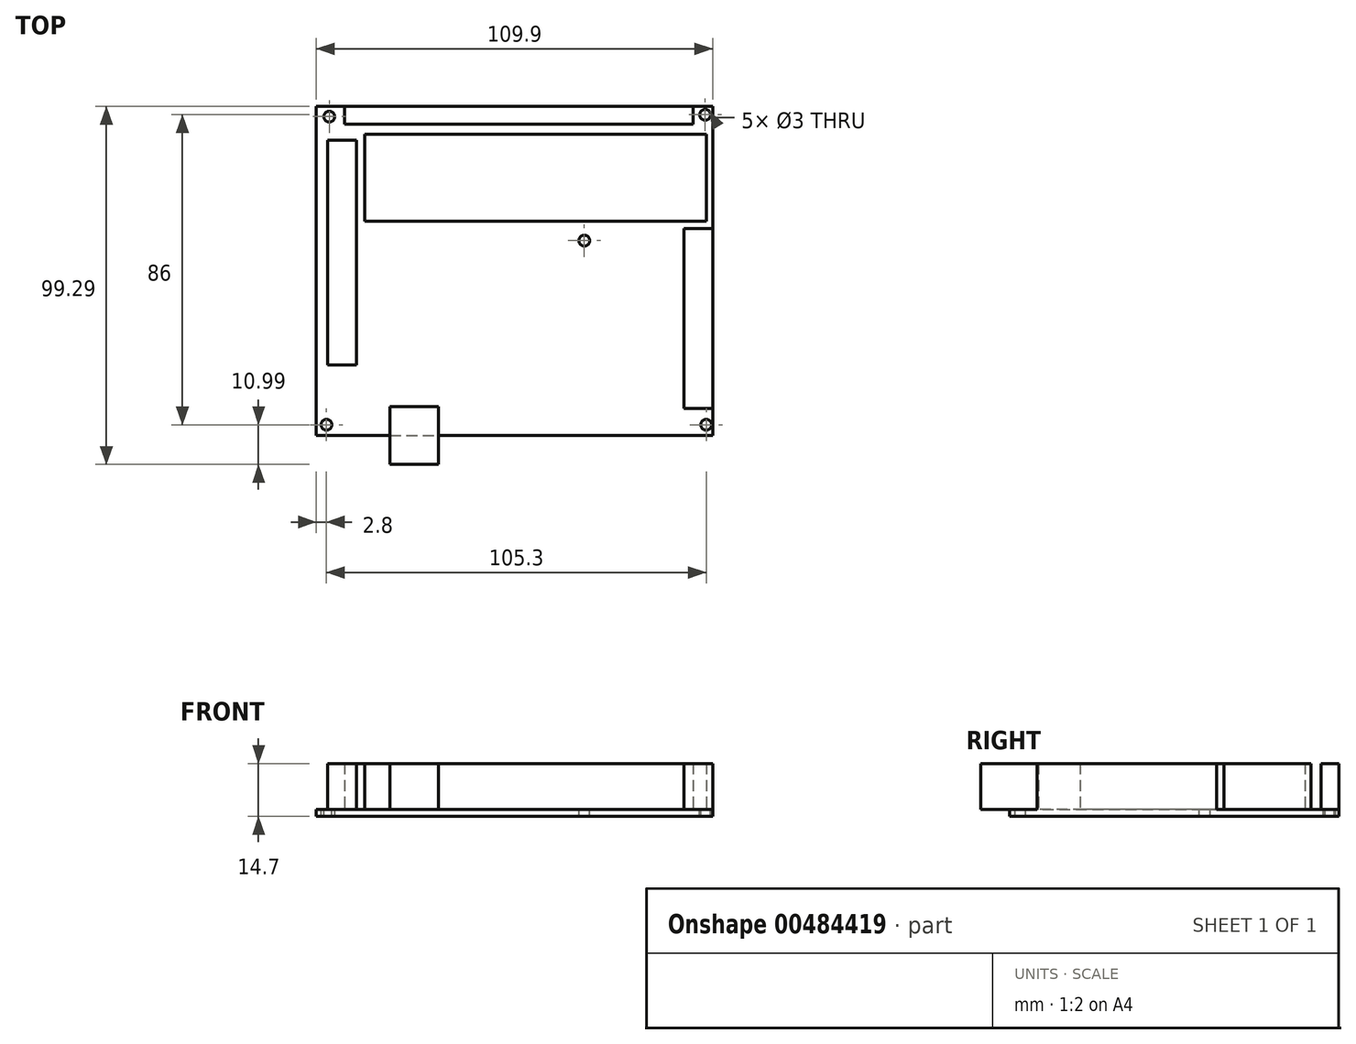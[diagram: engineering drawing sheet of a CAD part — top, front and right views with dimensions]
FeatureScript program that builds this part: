
annotation { "Feature Type Name" : "Feature", "Feature Type Description" : "" }
export const myFeature = defineFeature(function(context is Context, id is Id, definition is map)
    precondition{}
    {
        {
            var Q0;
            Q0=qCreatedBy(makeId("Top.planeOp"),FACE);
            var sketch = newSketch(context, id + "F0", { "sketchPlane" : qUnion([Q0])});
            skLineSegment(sketch, "E0.bottom", {"start": v(0, 0) * mm, "end": v(109.9, 0) * mm});
            skLineSegment(sketch, "E0.top", {"start": v(0, 91.3) * mm, "end": v(109.9, 91.3) * mm});
            skLineSegment(sketch, "E0.left", {"start": v(0, 0) * mm, "end": v(0, 91.3) * mm});
            skLineSegment(sketch, "E0.right", {"start": v(109.9, 0) * mm, "end": v(109.9, 91.3) * mm});
            skSolve(sketch);
        }
        {
            var Q0;
            Q0 = qSketchRegion(id + "F0", true);
            extrude(context, id + "F1", {"entities" : qUnion([Q0]), "depth" : 2 * mm, "offsetDistance" : 25.4 * mm});
        }
        {
            var Q0;
            Q0=makeQuery(id+"F1.opExtrude","CAP_FACE",FACE,{"disambiguationData":[OSD([sQuery(id+"F0.wireOp",EDGE,"E0.bottom"),sQuery(id+"F0.wireOp",EDGE,"E0.top"),sQuery(id+"F0.wireOp",EDGE,"E0.left"),sQuery(id+"F0.wireOp",EDGE,"E0.right")])],"isStart":false});
            var sketch = newSketch(context, id + "F2", { "sketchPlane" : qUnion([Q0])});
            skCircle(sketch, "E1", {"center": v(3.6, 88.5) * mm, "radius": 1.5 * mm});
            skCircle(sketch, "E2", {"center": v(108.1, 3) * mm, "radius": 1.5 * mm});
            skCircle(sketch, "E3", {"center": v(107.8, 89) * mm, "radius": 1.5 * mm});
            skCircle(sketch, "E4", {"center": v(2.8, 3) * mm, "radius": 1.5 * mm});
            skCircle(sketch, "E5", {"center": v(74.3, 54.1) * mm, "radius": 1.5 * mm});
            skSolve(sketch);
        }
        {
            var Q0;
            Q0 = qSketchRegion(id + "F2", true);
            extrude(context, id + "F3", {"entities" : qUnion([Q0]), "operationType" : NewBodyOperationType.REMOVE, "oppositeDirection" : true, "depth" : 25.4 * mm, "offsetDistance" : 25.4 * mm});
        }
        {
            var Q0;
            Q0=makeQuery(id+"F1.opExtrude","CAP_FACE",FACE,{"disambiguationData":[OSD([sQuery(id+"F0.wireOp",EDGE,"E0.bottom"),sQuery(id+"F0.wireOp",EDGE,"E0.top"),sQuery(id+"F0.wireOp",EDGE,"E0.left"),sQuery(id+"F0.wireOp",EDGE,"E0.right")])],"isStart":false});
            var sketch = newSketch(context, id + "F4", { "sketchPlane" : qUnion([Q0]), "disableImprinting" : false});
            skLineSegment(sketch, "E6.bottom", {"start": v(20.39, 8.06) * mm, "end": v(33.82, 8.06) * mm});
            skLineSegment(sketch, "E6.top", {"start": v(20.39, -7.99) * mm, "end": v(33.82, -7.99) * mm});
            skLineSegment(sketch, "E6.left", {"start": v(20.39, 8.06) * mm, "end": v(20.39, -7.99) * mm});
            skLineSegment(sketch, "E6.right", {"start": v(33.82, 8.06) * mm, "end": v(33.82, -7.99) * mm});
            skSolve(sketch);
        }
        {
            var Q0;
            Q0 = qSketchRegion(id + "F4", true);
            extrude(context, id + "F5", {"entities" : qUnion([Q0]), "operationType" : NewBodyOperationType.ADD, "depth" : 12.7 * mm, "offsetDistance" : 25.4 * mm});
        }
        {
            var Q0;
            Q0=makeQuery(id+"F1.opExtrude","CAP_FACE",FACE,{"disambiguationData":[OSD([sQuery(id+"F0.wireOp",EDGE,"E0.bottom"),sQuery(id+"F0.wireOp",EDGE,"E0.top"),sQuery(id+"F0.wireOp",EDGE,"E0.left"),sQuery(id+"F0.wireOp",EDGE,"E0.right")])],"isStart":false});
            var sketch = newSketch(context, id + "F6", { "sketchPlane" : qUnion([Q0])});
            skLineSegment(sketch, "E7.bottom", {"start": v(3.2, 81.95) * mm, "end": v(11.14, 81.95) * mm});
            skLineSegment(sketch, "E7.top", {"start": v(3.2, 19.55) * mm, "end": v(11.14, 19.55) * mm});
            skLineSegment(sketch, "E7.left", {"start": v(3.2, 81.95) * mm, "end": v(3.2, 19.55) * mm});
            skLineSegment(sketch, "E7.right", {"start": v(11.14, 81.95) * mm, "end": v(11.14, 19.55) * mm});
            skSolve(sketch);
        }
        {
            var Q0;
            Q0 = qSketchRegion(id + "F6", true);
            extrude(context, id + "F7", {"entities" : qUnion([Q0]), "operationType" : NewBodyOperationType.ADD, "depth" : 12.7 * mm, "offsetDistance" : 25.4 * mm});
        }
        {
            var Q0;
            Q0=makeQuery(id+"F1.opExtrude","CAP_FACE",FACE,{"disambiguationData":[OSD([sQuery(id+"F0.wireOp",EDGE,"E0.bottom"),sQuery(id+"F0.wireOp",EDGE,"E0.top"),sQuery(id+"F0.wireOp",EDGE,"E0.left"),sQuery(id+"F0.wireOp",EDGE,"E0.right")])],"isStart":false});
            var sketch = newSketch(context, id + "F8", { "sketchPlane" : qUnion([Q0]), "disableImprinting" : false});
            skLineSegment(sketch, "E8.bottom", {"start": v(101.93, 57.44) * mm, "end": v(109.9, 57.44) * mm});
            skLineSegment(sketch, "E8.top", {"start": v(101.93, 7.58) * mm, "end": v(109.9, 7.58) * mm});
            skLineSegment(sketch, "E8.left", {"start": v(101.93, 57.44) * mm, "end": v(101.93, 7.58) * mm});
            skLineSegment(sketch, "E8.right", {"start": v(109.9, 57.44) * mm, "end": v(109.9, 7.58) * mm});
            skLineSegment(sketch, "E9.bottom", {"start": v(108.2, 83.57) * mm, "end": v(13.37, 83.57) * mm});
            skLineSegment(sketch, "E9.top", {"start": v(108.2, 59.42) * mm, "end": v(13.37, 59.42) * mm});
            skLineSegment(sketch, "E9.left", {"start": v(108.2, 83.57) * mm, "end": v(108.2, 59.42) * mm});
            skLineSegment(sketch, "E9.right", {"start": v(13.37, 83.57) * mm, "end": v(13.37, 59.42) * mm});
            skLineSegment(sketch, "E10.bottom", {"start": v(7.88, 91.3) * mm, "end": v(104.5, 91.3) * mm});
            skLineSegment(sketch, "E10.top", {"start": v(7.88, 86.44) * mm, "end": v(104.5, 86.44) * mm});
            skLineSegment(sketch, "E10.left", {"start": v(7.88, 91.3) * mm, "end": v(7.88, 86.44) * mm});
            skLineSegment(sketch, "E10.right", {"start": v(104.5, 91.3) * mm, "end": v(104.5, 86.44) * mm});
            skSolve(sketch);
        }
        {
            var Q0;
            Q0 = qSketchRegion(id + "F8", true);
            extrude(context, id + "F9", {"entities" : qUnion([Q0]), "operationType" : NewBodyOperationType.ADD, "depth" : 12.7 * mm, "offsetDistance" : 25.4 * mm});
        }
    });
